# Revit family: Door-Rolling-Grille_300_FaceOfWallMount-CornelIron
name_source: partatom
category: Doors
revit_build: Autodesk Revit Architecture 2016 (Build: 20150220_1215(x64)
units: mm (PartAtom-declared; Revit-internal decimal feet)

## family parameters
Always vertical = Yes
Cut with Voids When Loaded = No
Host = Wall
OmniClass Number = 23.30.10.17.17
OmniClass Title = Folding Doors and Grilles
Room Calculation Point = No
Shared = No

## types (1)
- Motor Operated, Aluminium (Mill Finish), 9" Vertical Spacing
    # Of Brick Grills = 32
    # Of Straight Grills = 32
    04 CSI = 08 33 00
    95 CSI = 08330
    Assembly Code = B2030410
    Bottom Bar = Aluminum, mill finish
    Coil Dimension Note = 13” to 20” - Consult CornellIron when dimensions are critical.
    Control Box Height = 4' - 0"
    Control Box Offset = 2' - 0"
    Curtain Brick = No
    Curtain Rods 2In OC Standard = Aluminum, mill finish
    Curtain Spacing Vertical Chains 3In OC = No
    Curtain Spacing Vertical Chains 6In OC = No
    Curtain Spacing Vertical Chains 9In OC = Yes
    Curtain Straight = Yes
    Description = Built to order, open curtain grilles provide security, visual access of separated areas.
    Distributor Locator = http://www.cornelliron.com
    Drip Extension = 0' - 9"
    From Coil Side Operate on Left = Yes
    From Coil Side Operate on Right = No
    Function = Interior
    Gard Width = 8' - 1 7/16"
    Guides = Aluminum, mill finish
    Hand Crank = No
    Height = 10' - 0"
    Hood = Aluminum, mill finish
    Horizontal Spacing = 0' - 9"
    Jamb Dimension Note = 5” to 6 1/2” wide. Consult CornellIron when dimensions are critical.
    Jamb Height = 10' - 9"
    LEED Information = http://www.CornellIron.com
    Manufacturer = CornellIron
    Model = 300
    Motor = No
    Mounting = Face of Wall
    Operator Height = 5' - 4"
    Operator Width = 9' - 1 5/8"
    Optional aluminum, color anodized finish = No
    Product Options = Open Curtain Brick Pattern, Glazed Curtain, Injection molded link curtain. High Cycle Construction (>20/day)
    Representative Disclaimer = CornellIron products are sold and installed through a nationwide network of independent distributors.
    Rough Height = 7' - 10 1/2"
    Shutter Height = 10' - 9"
    Shutter Width = 7' - 11 15/16"
    Sizing Disclaimer = Openings up to 40’ wide x 20’ high standard construction. Consult CornellIron for larger sizes.
    Subcategory = Roll Up
    URL = https://www.cornelliron.com
    URL Photographs = https://www.cornelliron.com
    URL Specifications = http://www.cornelliron.com
    Vertical Spacing = 0' - 2"
    Wall Closure = By host
    Wall Construction = Self supporting tubes, Masonry, Steel or Wood
    Width = 8' - 0"

## geometry (parser evidence)
native form markers: Blend x16, Sweep x34
no freeform markers — native parametric forms only
